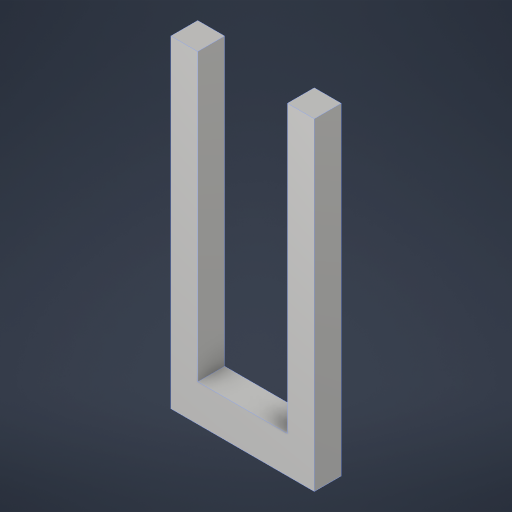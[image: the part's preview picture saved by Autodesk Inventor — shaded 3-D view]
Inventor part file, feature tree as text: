
AUTODESK INVENTOR PART (.ipt)
format: ipt  version: 2024.2 (Build 282272000, 272)  size: 231,424 bytes
history: native  units: in
note: dims shown in document units (in); Inventor stores cm internally (conversion verified against a paired STEP export)
features: extrude x2, sketch x2, projected_geometry x1
ambient origin geometry x8: Origin, YZ Plane, XZ Plane, XY Plane, X Axis, Y Axis, Z Axis, Center Point
bodies: Solid1 (feature_tree)
feature tree (5):
  extrude  "Extrusion1"  Depth=36.0in
  extrude  "Extrusion2"  Depth=4.1061in
  sketch  "Sketch1"  dims[d0=16.0in d1=36.0in]
  sketch  "Sketch2"  dims[d2=3.0in d3=0.0in d4=4.1061in d5=3.0in d6=3.0in d7=1.0in d8=0.0in]
  projected_geometry  "Project Cut Edges1"
